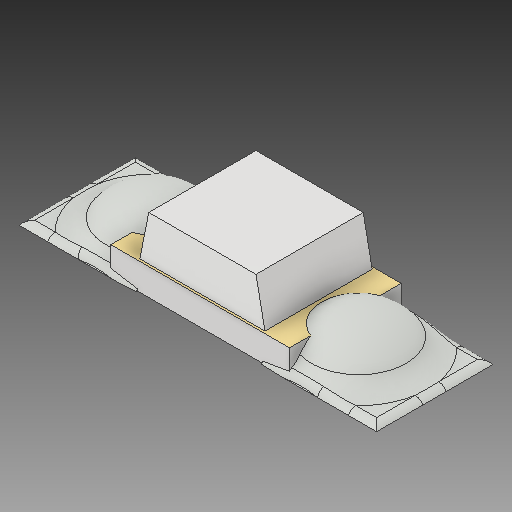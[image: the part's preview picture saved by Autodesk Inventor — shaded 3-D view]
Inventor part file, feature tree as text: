
AUTODESK INVENTOR PART (.ipt)
format: ipt  version: 2019 (Build 230136000, 136)  size: 218,112 bytes
history: native  units: in
note: dims shown in document units (in); Inventor stores cm internally (conversion verified against a paired STEP export)
features: mirror x1, other x1
ambient origin geometry x8: Origin, YZ Plane, XZ Plane, XY Plane, X Axis, Y Axis, Z Axis, Center Point
bodies: Solid1 (feature_tree), Solid2 (feature_tree)
feature tree (2):
  mirror  "Mirror3"
  other  "Boss-Extrude5"
